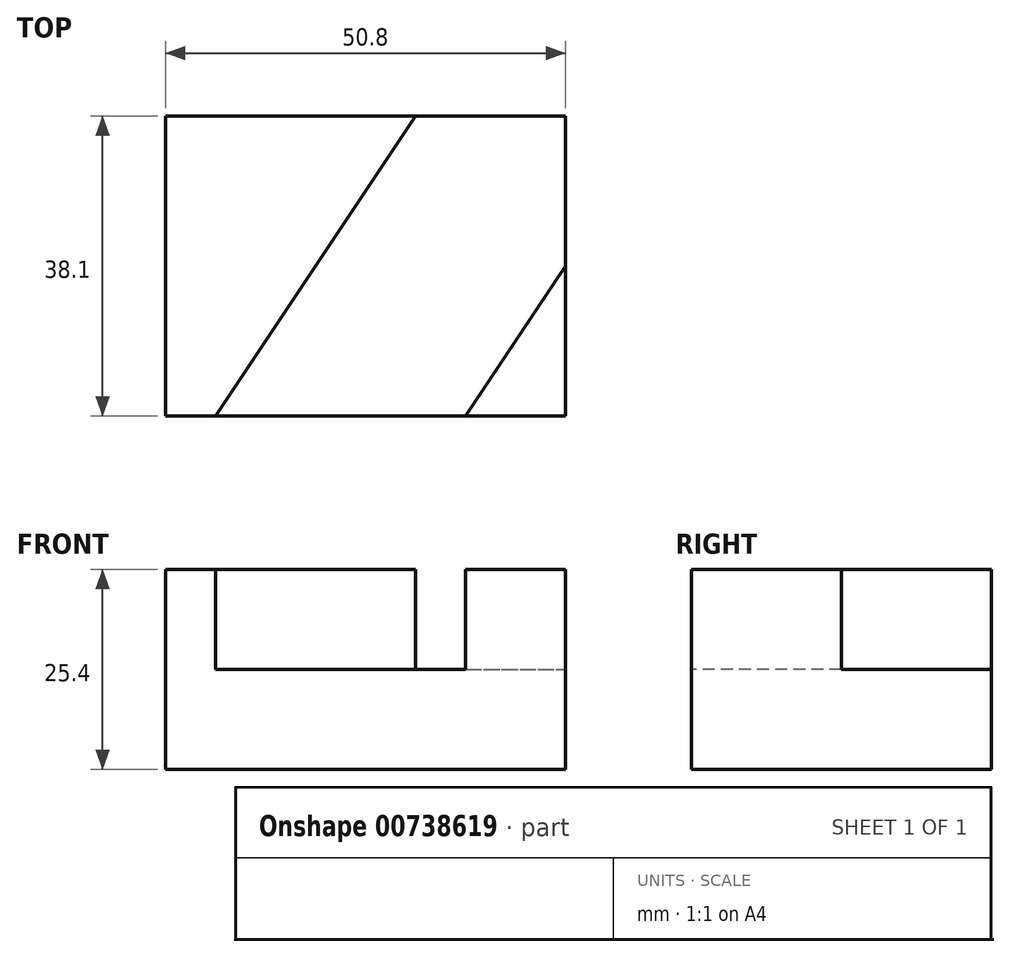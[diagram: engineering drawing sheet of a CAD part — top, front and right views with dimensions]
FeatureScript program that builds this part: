
annotation { "Feature Type Name" : "Feature", "Feature Type Description" : "" }
export const myFeature = defineFeature(function(context is Context, id is Id, definition is map)
    precondition{}
    {
        {
            var Q0;
            Q0=qCreatedBy(makeId("Top.planeOp"),FACE);
            var sketch = newSketch(context, id + "F0", { "sketchPlane" : qUnion([Q0])});
            skLineSegment(sketch, "E0.bottom", {"start": v(0, 0) * mm, "end": v(50.8, 0) * mm});
            skLineSegment(sketch, "E0.top", {"start": v(0, 38.1) * mm, "end": v(50.8, 38.1) * mm});
            skLineSegment(sketch, "E0.left", {"start": v(0, 0) * mm, "end": v(0, 38.1) * mm});
            skLineSegment(sketch, "E0.right", {"start": v(50.8, 0) * mm, "end": v(50.8, 38.1) * mm});
            skSolve(sketch);
        }
        {
            var Q0;
            Q0 = qSketchRegion(id + "F0", true);
            extrude(context, id + "F1", {"entities" : qUnion([Q0]), "depth" : 25.4 * mm, "offsetDistance" : 25.4 * mm});
        }
        {
            var Q0;
            Q0=makeQuery(id+"F1.opExtrude","CAP_FACE",FACE,{"disambiguationData":[OSD([sQuery(id+"F0.wireOp",EDGE,"E0.bottom"),sQuery(id+"F0.wireOp",EDGE,"E0.top"),sQuery(id+"F0.wireOp",EDGE,"E0.left"),sQuery(id+"F0.wireOp",EDGE,"E0.right")])],"isStart":false});
            var sketch = newSketch(context, id + "F2", { "sketchPlane" : qUnion([Q0])});
            skLineSegment(sketch, "E1", {"start": v(0, 0) * mm, "end": v(6.35, 0) * mm});
            skLineSegment(sketch, "E2", {"start": v(50.8, 38.1) * mm, "end": v(31.75, 38.1) * mm});
            skLineSegment(sketch, "E3", {"start": v(50.8, 0) * mm, "end": v(38.1, 0) * mm});
            skLineSegment(sketch, "E4", {"start": v(50.8, 0) * mm, "end": v(50.8, 19.05) * mm});
            skLineSegment(sketch, "E5", {"start": v(31.75, 38.1) * mm, "end": v(6.35, 0) * mm});
            skLineSegment(sketch, "E6", {"start": v(38.1, 0) * mm, "end": v(50.8, 19.05) * mm});
            skSolve(sketch);
        }
        {
            var Q0;
            {var subQ3=sQuery(id+"F2.wireOp",EDGE,"E2");Q0=makeQuery(id+"F2.imprint","IMPRINT",FACE,{"disambiguationData":[TD([[makeQuery(id+"F2.imprint","IMPRINT",EDGE,{"derivedFrom":subQ3}),-1.0]])]});}
            extrude(context, id + "F3", {"entities" : qUnion([Q0]), "operationType" : NewBodyOperationType.REMOVE, "oppositeDirection" : true, "depth" : 12.7 * mm, "offsetDistance" : 25.4 * mm});
        }
    });
